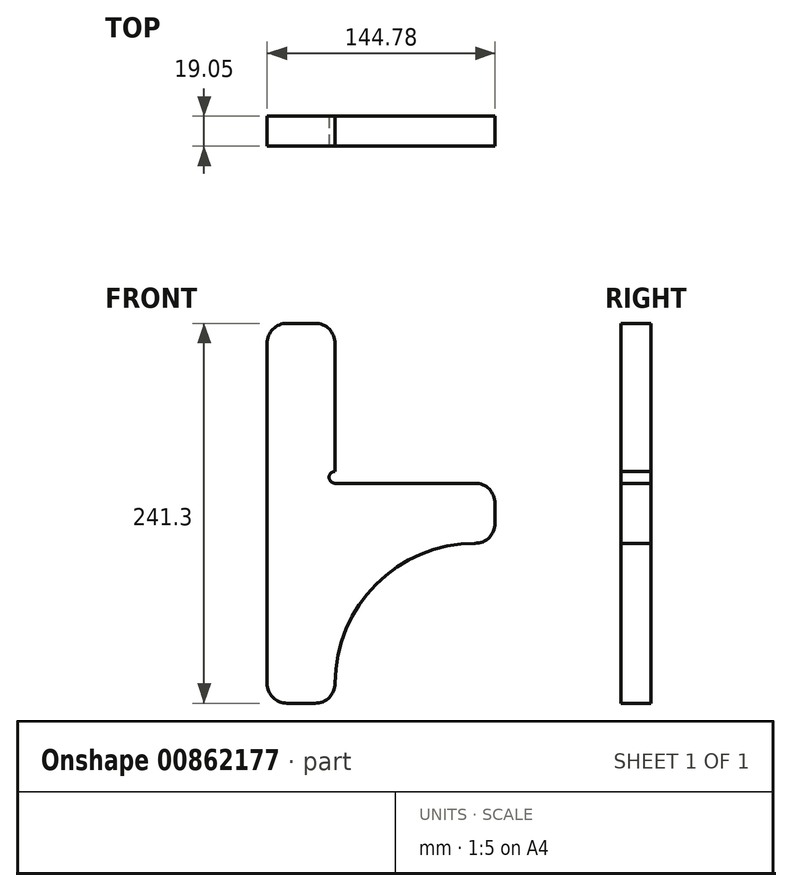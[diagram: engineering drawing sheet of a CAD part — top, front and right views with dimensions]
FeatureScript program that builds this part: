
annotation { "Feature Type Name" : "Feature", "Feature Type Description" : "" }
export const myFeature = defineFeature(function(context is Context, id is Id, definition is map)
    precondition{}
    {
        {
            var Q0;
            Q0=qCreatedBy(makeId("Front.planeOp"),FACE);
            var sketch = newSketch(context, id + "F0", { "sketchPlane" : qUnion([Q0])});
            skLineSegment(sketch, "E0", {"start": v(0, 508) * mm, "end": v(43.18, 508) * mm, "construction": true});
            skLineSegment(sketch, "E1", {"start": v(551.18, 273.05) * mm, "end": v(551.18, 234.95) * mm, "construction": true});
            skLineSegment(sketch, "E2", {"start": v(0, 0) * mm, "end": v(43.18, 0) * mm});
            skLineSegment(sketch, "E3", {"start": v(43.18, 0) * mm, "end": v(43.18, 101.6) * mm});
            skLineSegment(sketch, "E4", {"start": v(144.78, 101.6) * mm, "end": v(144.78, 139.7) * mm});
            skLineSegment(sketch, "E5", {"start": v(144.78, 139.7) * mm, "end": v(43.18, 139.7) * mm});
            skLineSegment(sketch, "E6", {"start": v(43.18, 241.3) * mm, "end": v(0, 241.3) * mm});
            skLineSegment(sketch, "E7", {"start": v(0, 241.3) * mm, "end": v(0, 0) * mm});
            skLineSegment(sketch, "E8", {"start": v(43.18, 241.3) * mm, "end": v(43.18, 139.7) * mm});
            skLineSegment(sketch, "E9", {"start": v(43.18, 101.6) * mm, "end": v(144.78, 101.6) * mm});
            skSolve(sketch);
        }
        {
            var Q0;
            Q0=makeQuery(id+"F0.imprint","IMPRINT",FACE,{"disambiguationData":[TD([[makeQuery(id+"F0.imprint","IMPRINT",EDGE,{"derivedFrom":sQuery(id+"F0.wireOp",EDGE,"E2")}),1.0]])]});
            extrude(context, id + "F1", {"entities" : qUnion([Q0]), "depth" : 19.05 * mm, "offsetDistance" : 25.4 * mm});
        }
        {
            var Q0;
            Q0=makeQuery(id+"F1.opExtrude","SWEPT_EDGE",EDGE,{"disambiguationData":[OSD([sQuery(id+"F0.wireOp",EDGE,"E3"),sQuery(id+"F0.wireOp",EDGE,"E9")])]});
            fillet(context, id + "F2", {"entities" : qUnion([Q0]), "radius" : 88.9 * mm, "tangentPropagation" : true, "allowEdgeOverflow" : false});
        }
        {
            var Q0;
            Q0=makeQuery(id+"F1.opExtrude","SWEPT_EDGE",EDGE,{"disambiguationData":[OSD([sQuery(id+"F0.wireOp",EDGE,"E4"),sQuery(id+"F0.wireOp",EDGE,"E5")])]});
            var Q1;
            Q1=makeQuery(id+"F1.opExtrude","SWEPT_EDGE",EDGE,{"disambiguationData":[OSD([sQuery(id+"F0.wireOp",EDGE,"E4"),sQuery(id+"F0.wireOp",EDGE,"E9")])]});
            var Q2;
            Q2=makeQuery(id+"F1.opExtrude","SWEPT_EDGE",EDGE,{"disambiguationData":[OSD([sQuery(id+"F0.wireOp",EDGE,"E2"),sQuery(id+"F0.wireOp",EDGE,"E3")])]});
            var Q3;
            Q3=makeQuery(id+"F1.opExtrude","SWEPT_EDGE",EDGE,{"disambiguationData":[OSD([sQuery(id+"F0.wireOp",EDGE,"E6"),sQuery(id+"F0.wireOp",EDGE,"E8")])]});
            var Q4;
            Q4=makeQuery(id+"F1.opExtrude","SWEPT_EDGE",EDGE,{"disambiguationData":[OSD([sQuery(id+"F0.wireOp",EDGE,"E2"),sQuery(id+"F0.wireOp",EDGE,"E7")])]});
            var Q5;
            Q5=makeQuery(id+"F1.opExtrude","SWEPT_EDGE",EDGE,{"disambiguationData":[OSD([sQuery(id+"F0.wireOp",EDGE,"E6"),sQuery(id+"F0.wireOp",EDGE,"E7")])]});
            fillet(context, id + "F3", {"entities" : qUnion([Q0, Q1, Q2, Q3, Q4, Q5]), "radius" : 12.7 * mm, "tangentPropagation" : true, "allowEdgeOverflow" : false});
        }
        {
            var Q0;
            Q0=makeQuery(id+"F1.opExtrude","CAP_FACE",FACE,{"disambiguationData":[OSD([sQuery(id+"F0.wireOp",EDGE,"E2"),sQuery(id+"F0.wireOp",EDGE,"E3"),sQuery(id+"F0.wireOp",EDGE,"E4"),sQuery(id+"F0.wireOp",EDGE,"E5"),sQuery(id+"F0.wireOp",EDGE,"E6"),sQuery(id+"F0.wireOp",EDGE,"E7"),sQuery(id+"F0.wireOp",EDGE,"E8"),sQuery(id+"F0.wireOp",EDGE,"E9")])],"isStart":false});
            var sketch = newSketch(context, id + "F4", { "sketchPlane" : qUnion([Q0])});
            skArc(sketch, "E10", {"start": v(43.18, 147.32) * mm, "mid": v(39.37, 143.5) * mm, "end": v(43.18, 139.7) * mm});
            skSolve(sketch);
        }
        {
            var Q0;
            {var subQ0=sQuery(id+"F4.wireOp",EDGE,"E10");Q0=makeQuery(id+"F4.imprint","IMPRINT",FACE,{"disambiguationData":[TD([[makeQuery(id+"F4.imprint","IMPRINT",EDGE,{"derivedFrom":subQ0}),1.0]])]});}
            extrude(context, id + "F5", {"entities" : qUnion([Q0]), "operationType" : NewBodyOperationType.REMOVE, "endBound" : BoundingType.THROUGH_ALL, "oppositeDirection" : true, "depth" : 25.4 * mm, "offsetDistance" : 25.4 * mm});
        }
    });
